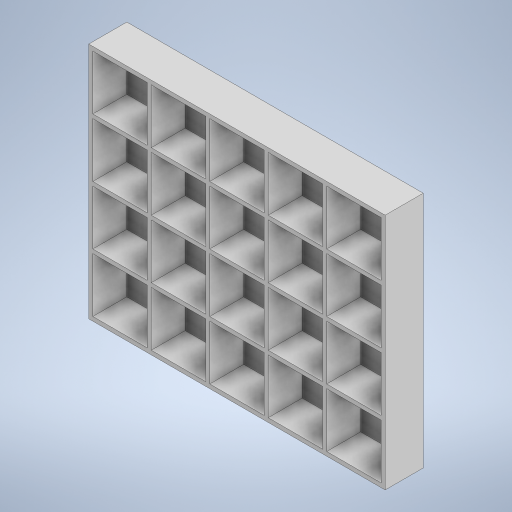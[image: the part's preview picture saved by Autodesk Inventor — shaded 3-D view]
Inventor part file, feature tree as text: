
AUTODESK INVENTOR PART (.ipt)
format: ipt  version: 2023.5 (Build 275446000, 446)  size: 372,736 bytes
history: native  units: in
note: dims shown in document units (in); Inventor stores cm internally (conversion verified against a paired STEP export)
features: extrude x2, sketch x2
ambient origin geometry x8: Origin, YZ Plane, XZ Plane, XY Plane, X Axis, Y Axis, Z Axis, Center Point
bodies: Solid1 (feature_tree)
feature tree (4):
  extrude  "Extrusion1"  Depth=6.8898in
  extrude  "Extrusion2"  TaperAngle=0.0deg  [1 undecoded]
  sketch  "Sketch1"  dims[d0=8.5827in d1=6.8898in]
  sketch  "Sketch2"  dims[d2=1.1024in d3=0.0in d4=1.5748in d5=0.1181in d6=0.1181in d7=1.5748in d8=1.9685in d10=1.6929in d11=1.5748in d13=1.6929in d16=0.9843in d17=0.0in]
note: 1 required parameter value undecoded (feature->parameter linkage not recoverable at this tier; creation-order binding heuristic only, values carry confidence <= 0.55)
